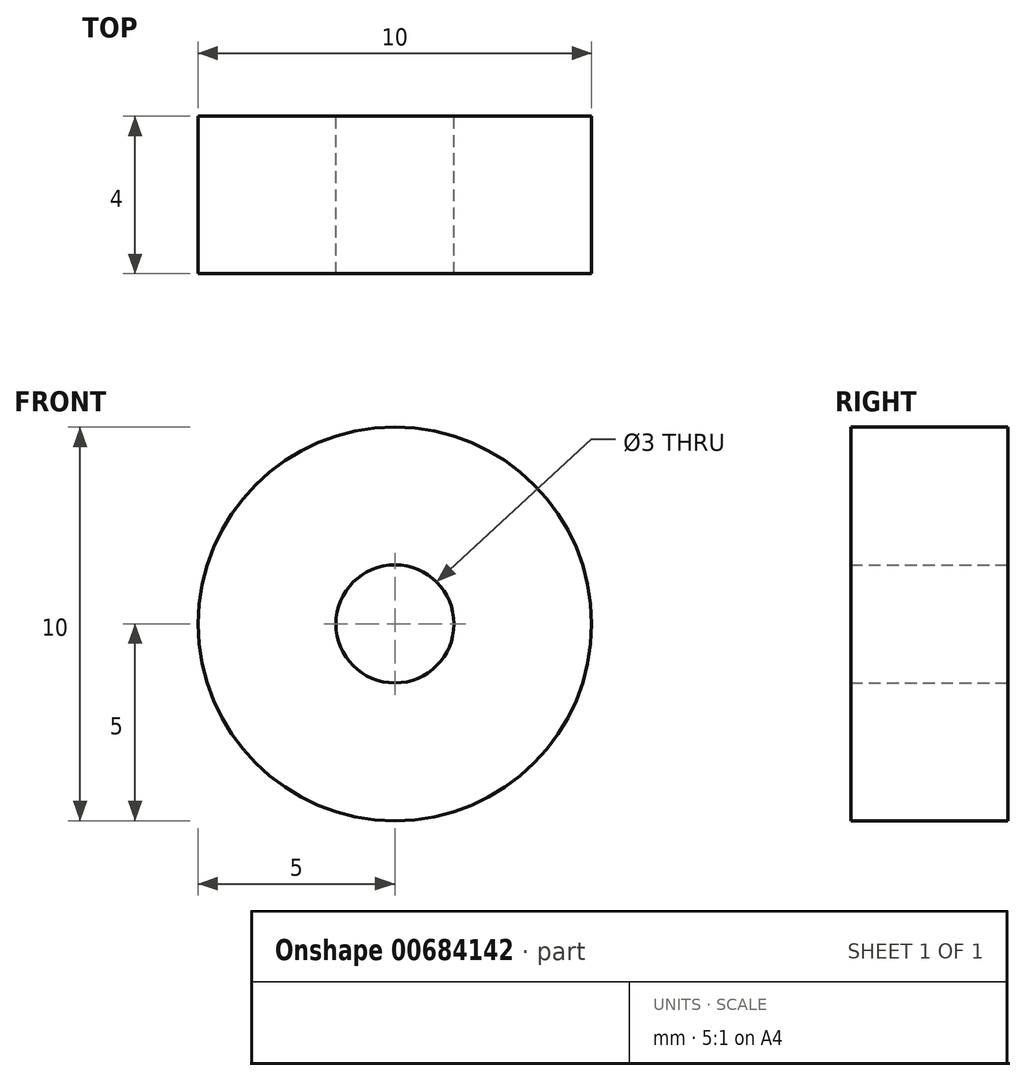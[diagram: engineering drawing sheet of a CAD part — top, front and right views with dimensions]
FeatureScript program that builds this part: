
annotation { "Feature Type Name" : "Feature", "Feature Type Description" : "" }
export const myFeature = defineFeature(function(context is Context, id is Id, definition is map)
    precondition{}
    {
        {
            var Q0;
            Q0=qCreatedBy(makeId("Front.planeOp"),FACE);
            var sketch = newSketch(context, id + "F0", { "sketchPlane" : qUnion([Q0])});
            skCircle(sketch, "E0", {"center": v(0, 0) * mm, "radius": 1.5 * mm});
            skCircle(sketch, "E1", {"center": v(0, 0) * mm, "radius": 5 * mm});
            skSolve(sketch);
        }
        {
            var Q0;
            Q0 = qSketchRegion(id + "F0", true);
            extrude(context, id + "F1", {"entities" : qUnion([Q0]), "depth" : 4 * mm, "offsetDistance" : 25 * mm});
        }
    });
